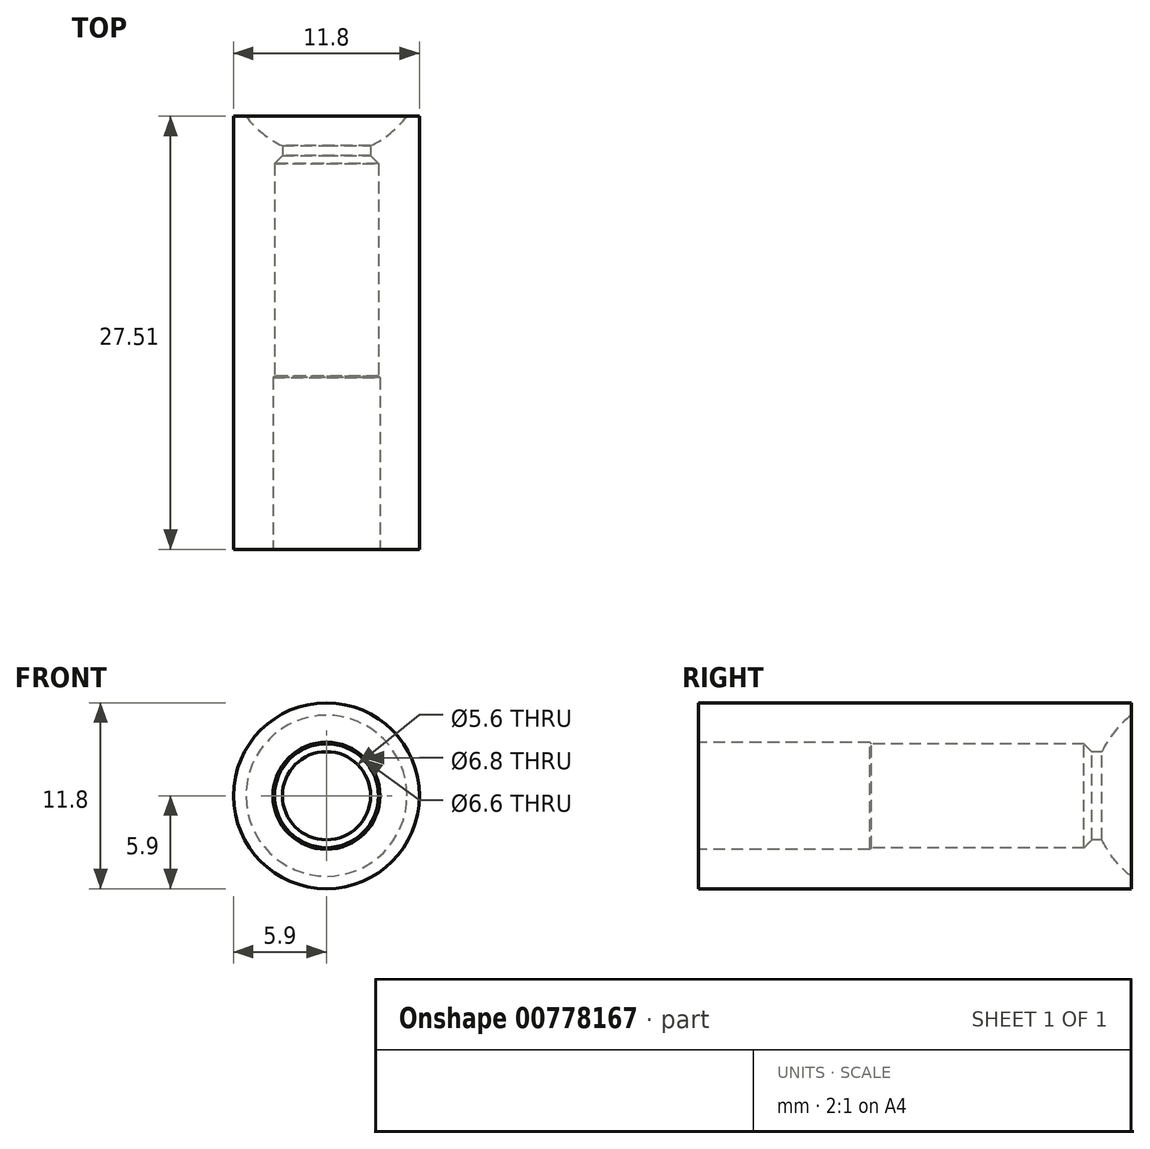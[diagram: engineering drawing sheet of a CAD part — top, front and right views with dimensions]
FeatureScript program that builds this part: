
annotation { "Feature Type Name" : "Feature", "Feature Type Description" : "" }
export const myFeature = defineFeature(function(context is Context, id is Id, definition is map)
    precondition{}
    {
        {
            var Q0;
            Q0=qCreatedBy(makeId("Right.planeOp"),FACE);
            var sketch = newSketch(context, id + "F0", { "sketchPlane" : qUnion([Q0])});
            skCircle(sketch, "E0", {"center": v(13.4, 0) * mm, "radius": 6.47 * mm});
            skLineSegment(sketch, "E1.bottom", {"start": v(-6.42, -3.3) * mm, "end": v(6.43, -3.3) * mm});
            skLineSegment(sketch, "E1.top", {"start": v(-6.42, 3.3) * mm, "end": v(6.43, 3.3) * mm});
            skLineSegment(sketch, "E1.left", {"start": v(-6.42, -3.3) * mm, "end": v(-6.42, 3.3) * mm});
            skLineSegment(sketch, "E1.right", {"start": v(6.43, -3.3) * mm, "end": v(6.43, 3.3) * mm});
            skPoint(sketch, "E1.middle", {"position": v(0, 0) * mm});
            skLineSegment(sketch, "E2.bottom", {"start": v(-7.07, -3.4) * mm, "end": v(-18.07, -3.4) * mm});
            skLineSegment(sketch, "E2.top", {"start": v(-7.07, 3.4) * mm, "end": v(-18.07, 3.4) * mm});
            skLineSegment(sketch, "E2.left", {"start": v(-7.07, -3.4) * mm, "end": v(-7.07, 3.4) * mm});
            skLineSegment(sketch, "E2.right", {"start": v(-18.07, -3.4) * mm, "end": v(-18.07, 3.4) * mm});
            skPoint(sketch, "E2.middle", {"position": v(-12.57, 0) * mm});
            skLineSegment(sketch, "E3", {"start": v(0, 0) * mm, "end": v(3, 0) * mm, "construction": true});
            skLineSegment(sketch, "E4", {"start": v(6.43, 1.5) * mm, "end": v(7.1, 1.5) * mm});
            skLineSegment(sketch, "E5", {"start": v(-18.07, 3.4) * mm, "end": v(-18.07, 5.9) * mm});
            skLineSegment(sketch, "E6", {"start": v(-18.07, 5.9) * mm, "end": v(10.73, 5.9) * mm});
            skLineSegment(sketch, "E7", {"start": v(-6.42, 3.3) * mm, "end": v(-7.07, 3.3) * mm});
            skLineSegment(sketch, "E8", {"start": v(9.43, 5.9) * mm, "end": v(9.43, 5.11) * mm});
            skLineSegment(sketch, "E9", {"start": v(6.93, 3.3) * mm, "end": v(6.93, 0) * mm});
            skPoint(sketch, "E9.endSnap0", {"position": v(6.43, 0) * mm});
            skLineSegment(sketch, "E10", {"start": v(6.93, 3.3) * mm, "end": v(6.43, 3.3) * mm});
            skLineSegment(sketch, "E11", {"start": v(6.42, 3.3) * mm, "end": v(6.93, 2.8) * mm});
            skLineSegment(sketch, "E12", {"start": v(6.93, 2.8) * mm, "end": v(7.56, 2.8) * mm});
            skSolve(sketch);
        }
        {
            var Q0;
            {var subQ0=sQuery(id+"F0.wireOp",EDGE,"E10");Q0=makeQuery(id+"F0.imprint","IMPRINT",FACE,{"disambiguationData":[TD([[makeQuery(id+"F0.imprint","IMPRINT",EDGE,{"derivedFrom":subQ0}),1.0]])]});}
            var Q1;
            Q1=makeQuery(id+"F0.imprint","IMPRINT",FACE,{"disambiguationData":[TD([[makeQuery(id+"F0.imprint","IMPRINT",EDGE,{"derivedFrom":sQuery(id+"F0.wireOp",EDGE,"E1.top")}),1.0]])]});
            var Q2;
            Q2=sQuery(id+"F0.wireOp",EDGE,"E3");
            revolve(context, id + "F1", {"surfaceOperationType" : NewSurfaceOperationType.NEW, "entities" : qUnion([Q0, Q1]), "axis" : qUnion([Q2]), "revolveType" : RevolveType.FULL});
        }
        {
            var Q0;
            Q0=makeQuery(id+"F1.opRevolve","SWEPT_EDGE",EDGE,{"disambiguationData":[OSD([sQuery(id+"F0.wireOp",EDGE,"E2.top"),sQuery(id+"F0.wireOp",EDGE,"E2.left")])]});
            chamfer(context, id + "F2", {"entities" : qUnion([Q0]), "width" : 0.1 * mm, "tangentPropagation" : true});
        }
    });
